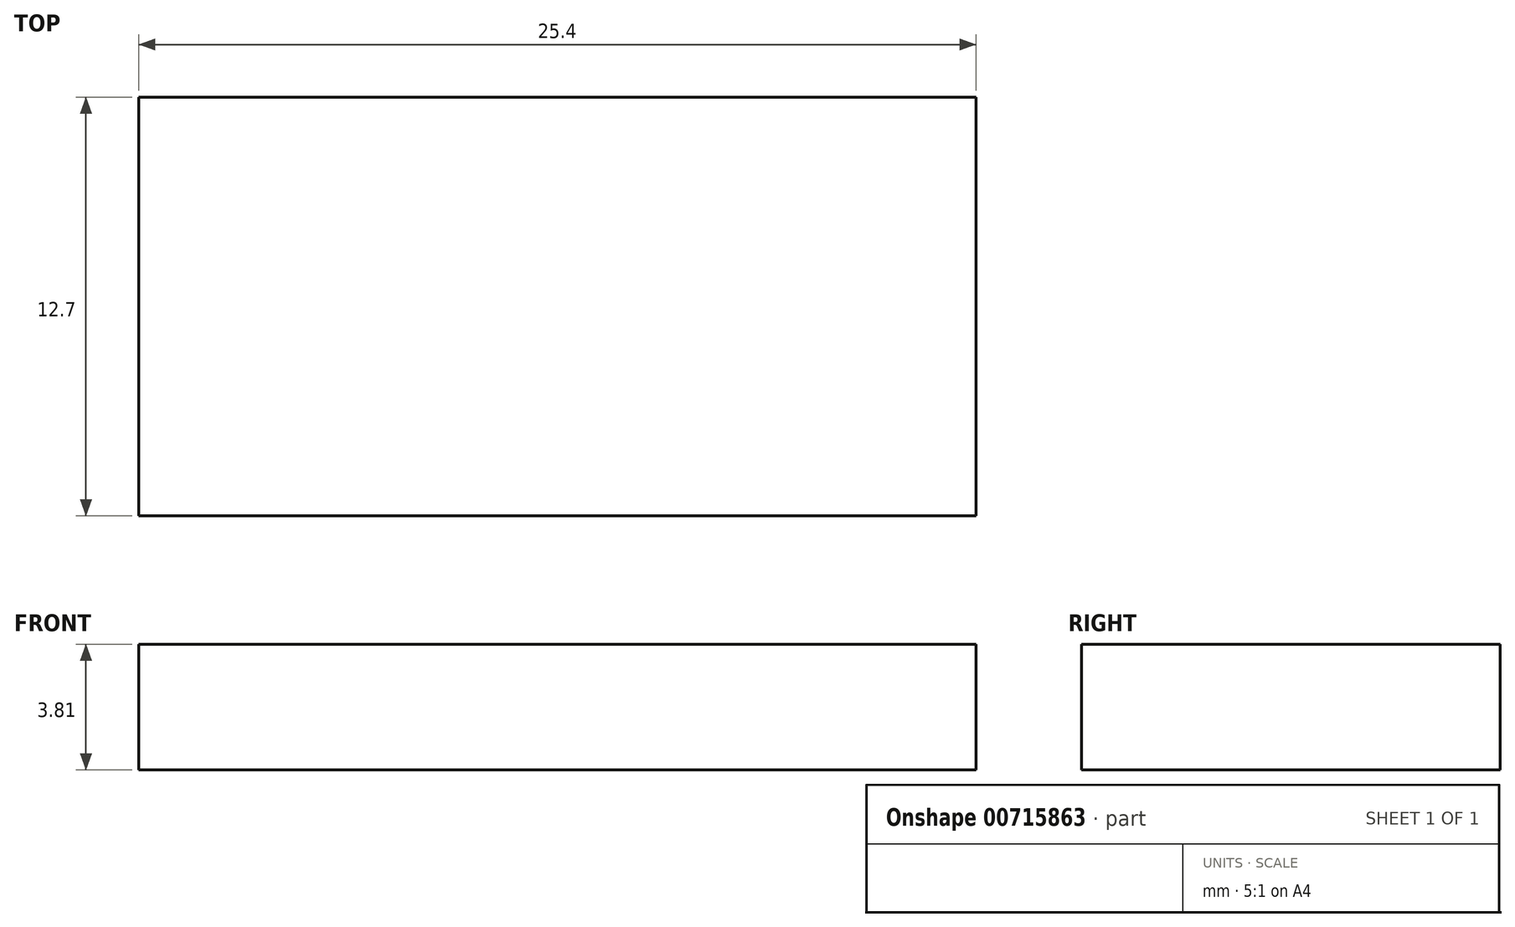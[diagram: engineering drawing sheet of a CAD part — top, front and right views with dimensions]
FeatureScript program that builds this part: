
annotation { "Feature Type Name" : "Feature", "Feature Type Description" : "" }
export const myFeature = defineFeature(function(context is Context, id is Id, definition is map)
    precondition{}
    {
        {
            var Q0;
            Q0=qCreatedBy(makeId("Top.planeOp"),FACE);
            var sketch = newSketch(context, id + "F0", { "sketchPlane" : qUnion([Q0])});
            skLineSegment(sketch, "E0", {"start": v(15.85, -11.85) * mm, "end": v(15.85, 0.85) * mm});
            skLineSegment(sketch, "E1", {"start": v(15.85, 0.85) * mm, "end": v(-9.55, 0.85) * mm});
            skLineSegment(sketch, "E2", {"start": v(-9.55, 0.85) * mm, "end": v(-9.55, -11.85) * mm});
            skPoint(sketch, "E3.start.orphan", {"position": v(0, -11.85) * mm});
            skLineSegment(sketch, "E4", {"start": v(-9.55, -11.85) * mm, "end": v(15.85, -11.85) * mm});
            skSolve(sketch);
        }
        {
            var Q0;
            Q0 = qSketchRegion(id + "F0", true);
            extrude(context, id + "F1", {"entities" : qUnion([Q0]), "oppositeDirection" : true, "depth" : 3.8 * mm, "offsetDistance" : 25.4 * mm});
        }
    });
